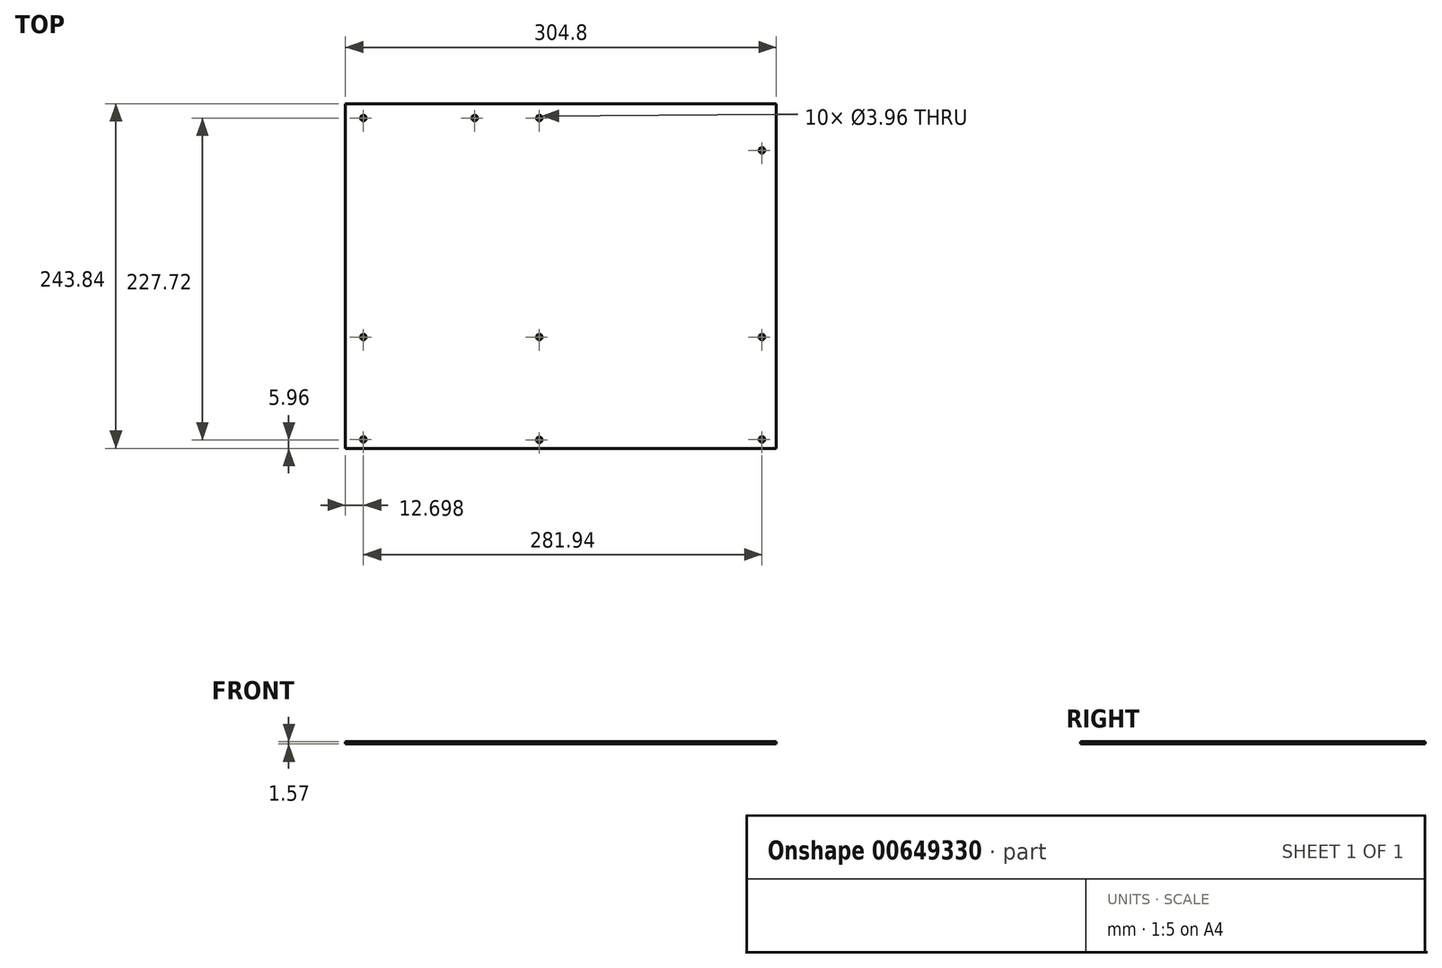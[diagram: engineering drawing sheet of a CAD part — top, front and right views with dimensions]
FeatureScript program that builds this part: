
annotation { "Feature Type Name" : "Feature", "Feature Type Description" : "" }
export const myFeature = defineFeature(function(context is Context, id is Id, definition is map)
    precondition{}
    {
        {
            var Q0;
            Q0=qCreatedBy(makeId("Top.planeOp"),FACE);
            var sketch = newSketch(context, id + "F0", { "sketchPlane" : qUnion([Q0])});
            skLineSegment(sketch, "E0.bottom", {"start": v(-152.4, 121.92) * mm, "end": v(152.4, 121.92) * mm});
            skLineSegment(sketch, "E0.top", {"start": v(-152.4, -121.92) * mm, "end": v(152.4, -121.92) * mm});
            skLineSegment(sketch, "E0.left", {"start": v(-152.4, 121.92) * mm, "end": v(-152.4, -121.92) * mm});
            skLineSegment(sketch, "E0.right", {"start": v(152.4, 121.92) * mm, "end": v(152.4, -121.92) * mm});
            skPoint(sketch, "E0.middle", {"position": v(0, 0) * mm});
            skCircle(sketch, "E1", {"center": v(-15.24, 111.76) * mm, "radius": 1.98 * mm});
            skCircle(sketch, "E2.0.1.0", {"center": v(-15.24, -43.18) * mm, "radius": 1.98 * mm});
            skCircle(sketch, "E2.0.2.0", {"center": v(-15.24, -115.96) * mm, "radius": 1.98 * mm});
            skCircle(sketch, "E3.1.0.0", {"center": v(-139.7, 111.76) * mm, "radius": 1.98 * mm});
            skCircle(sketch, "E3.1.0.1", {"center": v(-139.7, -43.18) * mm, "radius": 1.98 * mm});
            skCircle(sketch, "E3.1.0.2", {"center": v(-139.7, -115.57) * mm, "radius": 1.98 * mm});
            skCircle(sketch, "E4.1.0.0", {"center": v(142.24, -115.57) * mm, "radius": 1.98 * mm});
            skCircle(sketch, "E4.1.0.1", {"center": v(142.24, -43.18) * mm, "radius": 1.98 * mm});
            skCircle(sketch, "E5", {"center": v(-60.96, 111.76) * mm, "radius": 1.98 * mm});
            skCircle(sketch, "E6.1.0.1", {"center": v(142.24, 88.9) * mm, "radius": 1.98 * mm});
            skLineSegment(sketch, "E7", {"start": v(-139.7, 111.76) * mm, "end": v(-60.96, 111.76) * mm, "construction": true});
            skLineSegment(sketch, "E8", {"start": v(-15.24, 111.76) * mm, "end": v(-60.96, 111.76) * mm, "construction": true});
            skLineSegment(sketch, "E9", {"start": v(-139.7, 111.76) * mm, "end": v(-139.7, -43.18) * mm, "construction": true});
            skLineSegment(sketch, "E10", {"start": v(-139.7, -115.57) * mm, "end": v(-139.7, -43.18) * mm, "construction": true});
            skLineSegment(sketch, "E11", {"start": v(-15.24, -115.96) * mm, "end": v(-139.7, -115.57) * mm, "construction": true});
            skLineSegment(sketch, "E12", {"start": v(-15.24, -43.18) * mm, "end": v(-15.24, -115.96) * mm, "construction": true});
            skLineSegment(sketch, "E13", {"start": v(-15.24, -43.18) * mm, "end": v(-139.7, -43.18) * mm, "construction": true});
            skLineSegment(sketch, "E14", {"start": v(-15.24, 111.76) * mm, "end": v(-15.24, -43.18) * mm, "construction": true});
            skLineSegment(sketch, "E15", {"start": v(-15.24, -43.18) * mm, "end": v(142.24, -43.18) * mm, "construction": true});
            skLineSegment(sketch, "E16", {"start": v(142.24, -115.57) * mm, "end": v(142.24, -43.18) * mm, "construction": true});
            skLineSegment(sketch, "E17", {"start": v(142.24, -115.57) * mm, "end": v(-15.24, -115.96) * mm, "construction": true});
            skLineSegment(sketch, "E18", {"start": v(142.24, 88.9) * mm, "end": v(142.24, -43.18) * mm, "construction": true});
            skSolve(sketch);
        }
        {
            var Q0;
            Q0=makeQuery(id+"F0.imprint","IMPRINT",FACE,{"disambiguationData":[TD([[makeQuery(id+"F0.imprint","IMPRINT",EDGE,{"derivedFrom":sQuery(id+"F0.wireOp",EDGE,"E0.bottom")}),-1.0]])]});
            extrude(context, id + "F1", {"entities" : qUnion([Q0]), "oppositeDirection" : true, "depth" : 1.57 * mm, "offsetDistance" : 25.4 * mm});
        }
    });
